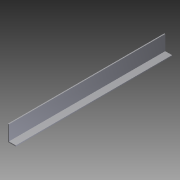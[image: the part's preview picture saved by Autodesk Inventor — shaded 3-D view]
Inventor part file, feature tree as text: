
AUTODESK INVENTOR PART (.ipt)
format: ipt  version: 2012 (Build 160160000, 160)  size: 76,800 bytes
history: native  units: in
note: dims shown in document units (in); Inventor stores cm internally (conversion verified against a paired STEP export)
features: extrude x1, sketch x1
ambient origin geometry x8: Origin, YZ Plane, XZ Plane, XY Plane, X Axis, Y Axis, Z Axis, Center Point
bodies: Solid1 (feature_tree)
feature tree (2):
  extrude  "Extrusion1"  Depth=1.0in
  sketch  "Sketch1"  dims[d0=2.0in d1=1.0in d2=0.125in d3=0.125in d4=19.75in d5=0.0in]
